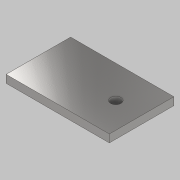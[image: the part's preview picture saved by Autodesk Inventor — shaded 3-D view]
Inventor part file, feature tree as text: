
AUTODESK INVENTOR PART (.ipt)
format: ipt  version: 2021 (Build 250183000, 183)  size: 97,280 bytes
history: native  units: mm
features: sketch x2, extrude x1, hole x1
ambient origin geometry x8: Origin, YZ Plane, XZ Plane, XY Plane, X Axis, Y Axis, Z Axis, Center Point
bodies: Solid1 (feature_tree)
feature tree (4):
  extrude  "base"  Depth=50.0mm
  hole  "mountingHole"  [1 undecoded]
  sketch  "Sketch1"  dims[d0=50.0mm d1=40.0mm]
  sketch  "Sketch2"  dims[d2=80.0mm d3=25.0mm d4=6.0mm d5=0.0mm d6=20.0mm d7=0.0mm d8=8.0mm d9=6.0mm d10=4.0mm d11=2.0mm d12=90.0deg d13=8.0mm d14=20.594885mm]
note: 1 required parameter value undecoded (feature->parameter linkage not recoverable at this tier; creation-order binding heuristic only, values carry confidence <= 0.55)
